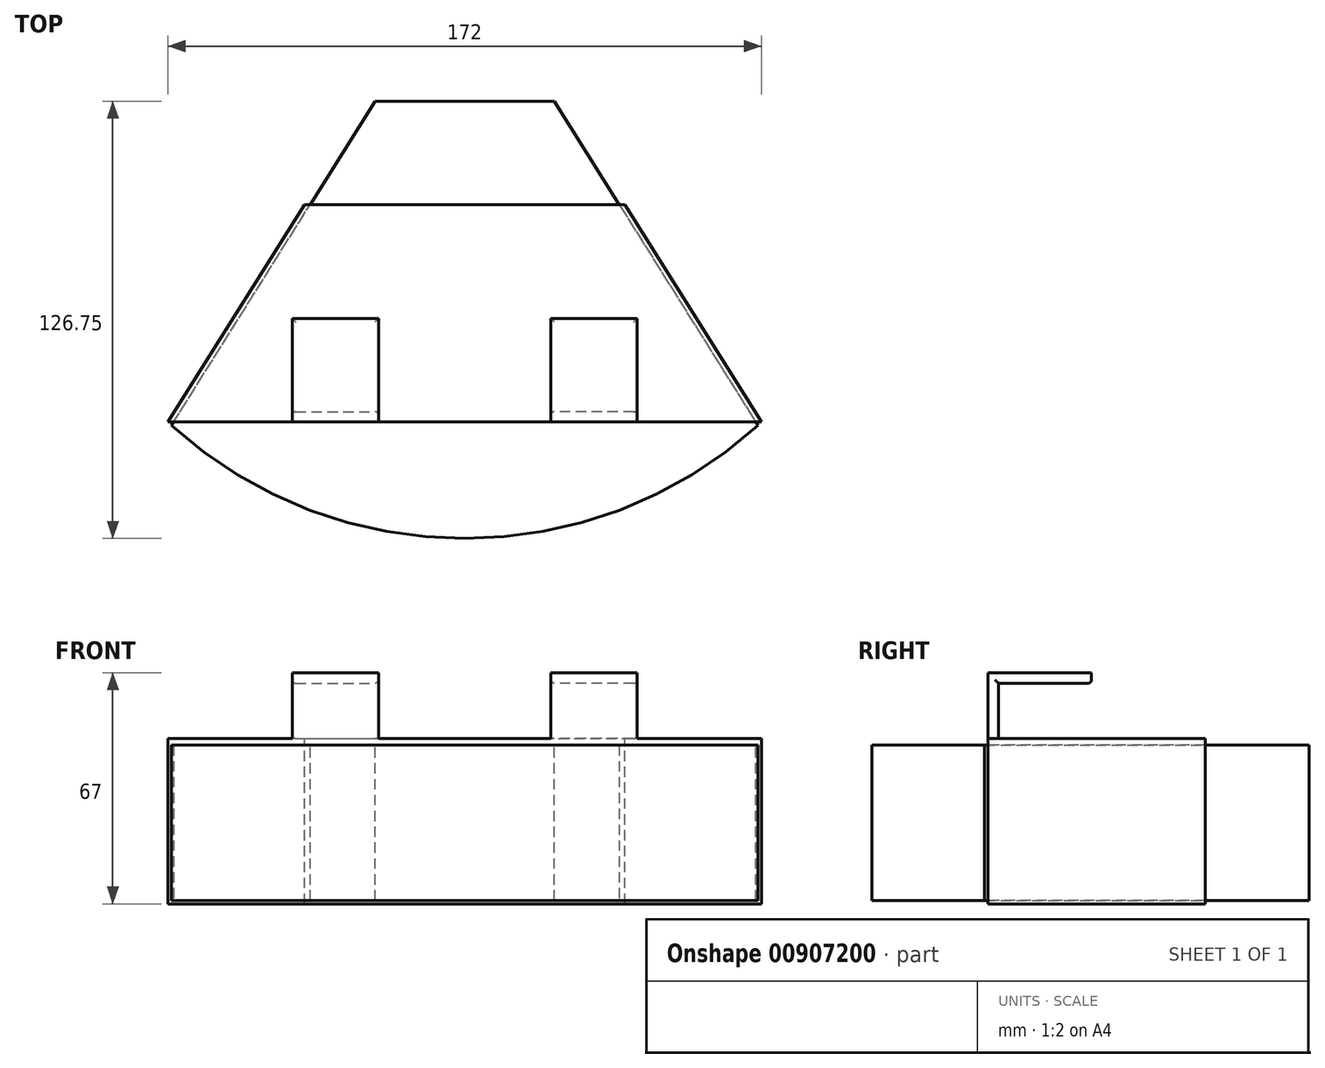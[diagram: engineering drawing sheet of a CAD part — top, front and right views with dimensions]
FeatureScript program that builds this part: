
annotation { "Feature Type Name" : "Feature", "Feature Type Description" : "" }
export const myFeature = defineFeature(function(context is Context, id is Id, definition is map)
    precondition{}
    {
        {
            var Q0;
            Q0=qCreatedBy(makeId("Top.planeOp"),FACE);
            var sketch = newSketch(context, id + "F0", { "sketchPlane" : qUnion([Q0])});
            skLineSegment(sketch, "E0", {"start": v(26, 0) * mm, "end": v(85, -94.02) * mm});
            skLineSegment(sketch, "E1", {"start": v(26, 0) * mm, "end": v(-26, 0) * mm});
            skLineSegment(sketch, "E2", {"start": v(-85, -94.02) * mm, "end": v(-26, 0) * mm});
            skArc(sketch, "E3", {"start": v(-85, -94.02) * mm, "mid": v(0, -126.75) * mm, "end": v(85, -94.02) * mm});
            skLineSegment(sketch, "E4", {"start": v(-85, -94.02) * mm, "end": v(85, -94.02) * mm, "construction": true});
            skSolve(sketch);
        }
        {
            var Q0;
            Q0 = qSketchRegion(id + "F0", true);
            extrude(context, id + "F1", {"entities" : qUnion([Q0]), "oppositeDirection" : true, "depth" : 45 * mm, "offsetDistance" : 25 * mm});
        }
        {
            var Q0;
            Q0=qCreatedBy(makeId("Top.planeOp"),FACE);
            var sketch = newSketch(context, id + "F2", { "sketchPlane" : qUnion([Q0])});
            skLineSegment(sketch, "E5", {"start": v(-86, -93.02) * mm, "end": v(-27, 1) * mm});
            skLineSegment(sketch, "E6", {"start": v(-27, 1) * mm, "end": v(27, 1) * mm});
            skLineSegment(sketch, "E7", {"start": v(27, 1) * mm, "end": v(86, -93.02) * mm});
            skLineSegment(sketch, "E8", {"start": v(86, -93.02) * mm, "end": v(-86, -93.02) * mm});
            skPoint(sketch, "E9", {"position": v(0, 1) * mm});
            skLineSegment(sketch, "E10", {"start": v(-46.45, -30) * mm, "end": v(46.45, -30) * mm});
            skSolve(sketch);
        }
        {
            var Q0;
            {var subQ0=sQuery(id+"F2.wireOp",EDGE,"E8");Q0=makeQuery(id+"F2.imprint","IMPRINT",FACE,{"disambiguationData":[TD([[makeQuery(id+"F2.imprint","IMPRINT",EDGE,{"derivedFrom":subQ0}),-1.0]])]});}
            var Q1;
            Q1=makeQuery(id+"F1.opExtrude","CAP_FACE",FACE,{"disambiguationData":[OSD([sQuery(id+"F0.wireOp",EDGE,"E0"),sQuery(id+"F0.wireOp",EDGE,"E1"),sQuery(id+"F0.wireOp",EDGE,"E2"),sQuery(id+"F0.wireOp",EDGE,"E3")])],"isStart":false});
            extrude(context, id + "F3", {"entities" : qUnion([Q0]), "endBound" : BoundingType.UP_TO_SURFACE, "oppositeDirection" : true, "depth" : 2 * mm, "endBoundEntityFace" : qUnion([Q1]), "hasOffset" : true, "offsetDistance" : 1 * mm, "offsetOppositeDirection" : true, "hasSecondDirection" : true, "secondDirectionOppositeDirection" : false, "secondDirectionDepth" : 2 * mm});
        }
        {
            var Q0;
            Q0=makeQuery(id+"F1.opExtrude","SWEPT_BODY",BODY,{"disambiguationData":[OSD([sQuery(id+"F0.wireOp",EDGE,"E0"),sQuery(id+"F0.wireOp",EDGE,"E1"),sQuery(id+"F0.wireOp",EDGE,"E2"),sQuery(id+"F0.wireOp",EDGE,"E3")])]});
            var Q1;
            Q1=makeQuery(id+"F3.opExtrude","SWEPT_BODY",BODY,{"disambiguationData":[OSD([sQuery(id+"F2.wireOp",EDGE,"E5"),sQuery(id+"F2.wireOp",EDGE,"E6"),sQuery(id+"F2.wireOp",EDGE,"E7"),sQuery(id+"F2.wireOp",EDGE,"E8")])]});
            booleanBodies(context, id + "F4", {"operationType" : BooleanOperationType.SUBTRACTION, "tools" : qUnion([Q0]), "targets" : qUnion([Q1]), "keepTools" : true});
        }
        {
            var Q0;
            Q0=qCreatedBy(makeId("Right.planeOp"),FACE);
            var sketch = newSketch(context, id + "F5", { "sketchPlane" : qUnion([Q0])});
            skLineSegment(sketch, "E11.0.0", {"start": v(-93.02, 2) * mm, "end": v(-30, 2) * mm, "construction": true});
            skLineSegment(sketch, "E11.0.2", {"start": v(-30, 2) * mm, "end": v(-93.02, 2) * mm, "construction": true});
            skLineSegment(sketch, "E12", {"start": v(-63.02, 18) * mm, "end": v(-63.02, 21) * mm});
            skLineSegment(sketch, "E13", {"start": v(-63.02, 21) * mm, "end": v(-93.02, 21) * mm});
            skLineSegment(sketch, "E14", {"start": v(-93.02, 21) * mm, "end": v(-93.02, 2) * mm});
            skLineSegment(sketch, "E15", {"start": v(-63.02, 18) * mm, "end": v(-90.02, 18) * mm});
            skLineSegment(sketch, "E16", {"start": v(-90.02, 2) * mm, "end": v(-90.02, 18) * mm});
            skLineSegment(sketch, "E17", {"start": v(-93.02, 2) * mm, "end": v(-90.02, 2) * mm});
            skSolve(sketch);
        }
        {
            var Q0;
            Q0 = qSketchRegion(id + "F5", true);
            extrude(context, id + "F6", {"entities" : qUnion([Q0]), "depth" : 50 * mm, "offsetDistance" : 25 * mm, "hasSecondDirection" : true, "secondDirectionOppositeDirection" : false, "secondDirectionDepth" : 25 * mm});
        }
        {
            var Q0;
            Q0=makeQuery(id+"F6.opExtrude","SWEPT_BODY",BODY,{"disambiguationData":[OSD([sQuery(id+"F5.wireOp",EDGE,"E12"),sQuery(id+"F5.wireOp",EDGE,"E13"),sQuery(id+"F5.wireOp",EDGE,"E14"),sQuery(id+"F5.wireOp",EDGE,"E15"),sQuery(id+"F5.wireOp",EDGE,"E16"),sQuery(id+"F5.wireOp",EDGE,"E17")])]});
            var Q1;
            Q1=qCreatedBy(makeId("Right.planeOp"),FACE);
            mirror(context, id + "F7", {"operationType" : NewBodyOperationType.ADD, "entities" : qUnion([Q0]), "mirrorPlane" : qUnion([Q1])});
        }
        {
            var Q0;
            Q0=makeQuery(id+"F7.opPattern","COPY",EDGE,{"derivedFrom":makeQuery(id+"F6.opExtrude","SWEPT_EDGE",EDGE,{"disambiguationData":[OSD([sQuery(id+"F5.wireOp",EDGE,"E12"),sQuery(id+"F5.wireOp",EDGE,"E15")])]}),"instanceName":"1"});
            var Q1;
            Q1=makeQuery(id+"F6.opExtrude","SWEPT_EDGE",EDGE,{"disambiguationData":[OSD([sQuery(id+"F5.wireOp",EDGE,"E12"),sQuery(id+"F5.wireOp",EDGE,"E15")])]});
            var Q2;
            Q2=makeQuery(id+"F6.opExtrude","CAP_EDGE",EDGE,{"disambiguationData":[OSD([sQuery(id+"F5.wireOp",EDGE,"E15")])],"isStart":false});
            var Q3;
            Q3=makeQuery(id+"F6.opExtrude","CAP_EDGE",EDGE,{"disambiguationData":[OSD([sQuery(id+"F5.wireOp",EDGE,"E15")])],"isStart":true});
            var Q4;
            Q4=makeQuery(id+"F7.opPattern","COPY",EDGE,{"derivedFrom":makeQuery(id+"F6.opExtrude","CAP_EDGE",EDGE,{"disambiguationData":[OSD([sQuery(id+"F5.wireOp",EDGE,"E15")])],"isStart":true}),"instanceName":"1"});
            var Q5;
            Q5=makeQuery(id+"F7.opPattern","COPY",EDGE,{"derivedFrom":makeQuery(id+"F6.opExtrude","CAP_EDGE",EDGE,{"disambiguationData":[OSD([sQuery(id+"F5.wireOp",EDGE,"E15")])],"isStart":false}),"instanceName":"1"});
            var Q6;
            Q6=makeQuery(id+"F7.opPattern","COPY",EDGE,{"derivedFrom":makeQuery(id+"F6.opExtrude","CAP_EDGE",EDGE,{"disambiguationData":[OSD([sQuery(id+"F5.wireOp",EDGE,"E16")])],"isStart":false}),"instanceName":"1"});
            var Q7;
            Q7=makeQuery(id+"F7.opPattern","COPY",EDGE,{"derivedFrom":makeQuery(id+"F6.opExtrude","CAP_EDGE",EDGE,{"disambiguationData":[OSD([sQuery(id+"F5.wireOp",EDGE,"E16")])],"isStart":true}),"instanceName":"1"});
            var Q8;
            Q8=makeQuery(id+"F6.opExtrude","CAP_EDGE",EDGE,{"disambiguationData":[OSD([sQuery(id+"F5.wireOp",EDGE,"E16")])],"isStart":true});
            var Q9;
            Q9=makeQuery(id+"F6.opExtrude","CAP_EDGE",EDGE,{"disambiguationData":[OSD([sQuery(id+"F5.wireOp",EDGE,"E16")])],"isStart":false});
            fillet(context, id + "F8", {"entities" : qUnion([Q0, Q1, Q2, Q3, Q4, Q5, Q6, Q7, Q8, Q9]), "radius" : 1 * mm, "tangentPropagation" : true, "allowEdgeOverflow" : false});
        }
    });
